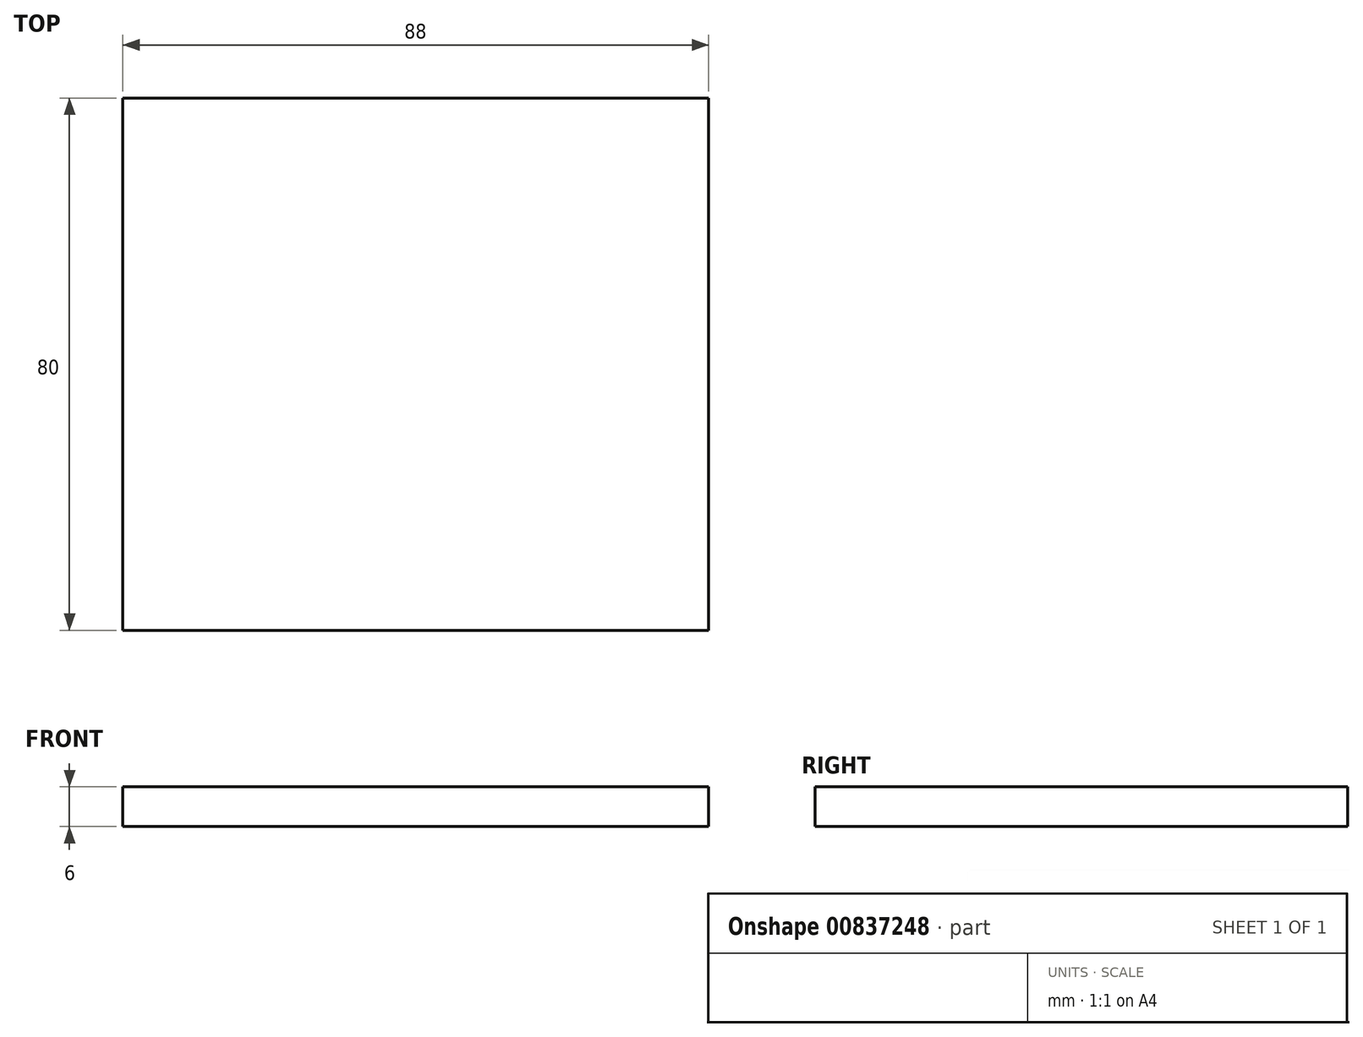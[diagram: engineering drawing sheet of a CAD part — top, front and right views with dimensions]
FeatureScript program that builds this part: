
annotation { "Feature Type Name" : "Feature", "Feature Type Description" : "" }
export const myFeature = defineFeature(function(context is Context, id is Id, definition is map)
    precondition{}
    {
        {
            var Q0;
            Q0=qCreatedBy(makeId("Top.planeOp"),FACE);
            var sketch = newSketch(context, id + "F0", { "sketchPlane" : qUnion([Q0])});
            skLineSegment(sketch, "E0.bottom", {"start": v(-44, 40) * mm, "end": v(44, 40) * mm});
            skLineSegment(sketch, "E0.top", {"start": v(-44, -40) * mm, "end": v(44, -40) * mm});
            skLineSegment(sketch, "E0.left", {"start": v(-44, 40) * mm, "end": v(-44, -40) * mm});
            skLineSegment(sketch, "E0.right", {"start": v(44, 40) * mm, "end": v(44, -40) * mm});
            skSolve(sketch);
        }
        {
            var Q0;
            Q0 = qSketchRegion(id + "F0", true);
            extrude(context, id + "F1", {"entities" : qUnion([Q0]), "depth" : 6 * mm, "offsetDistance" : 25.4 * mm});
        }
    });
